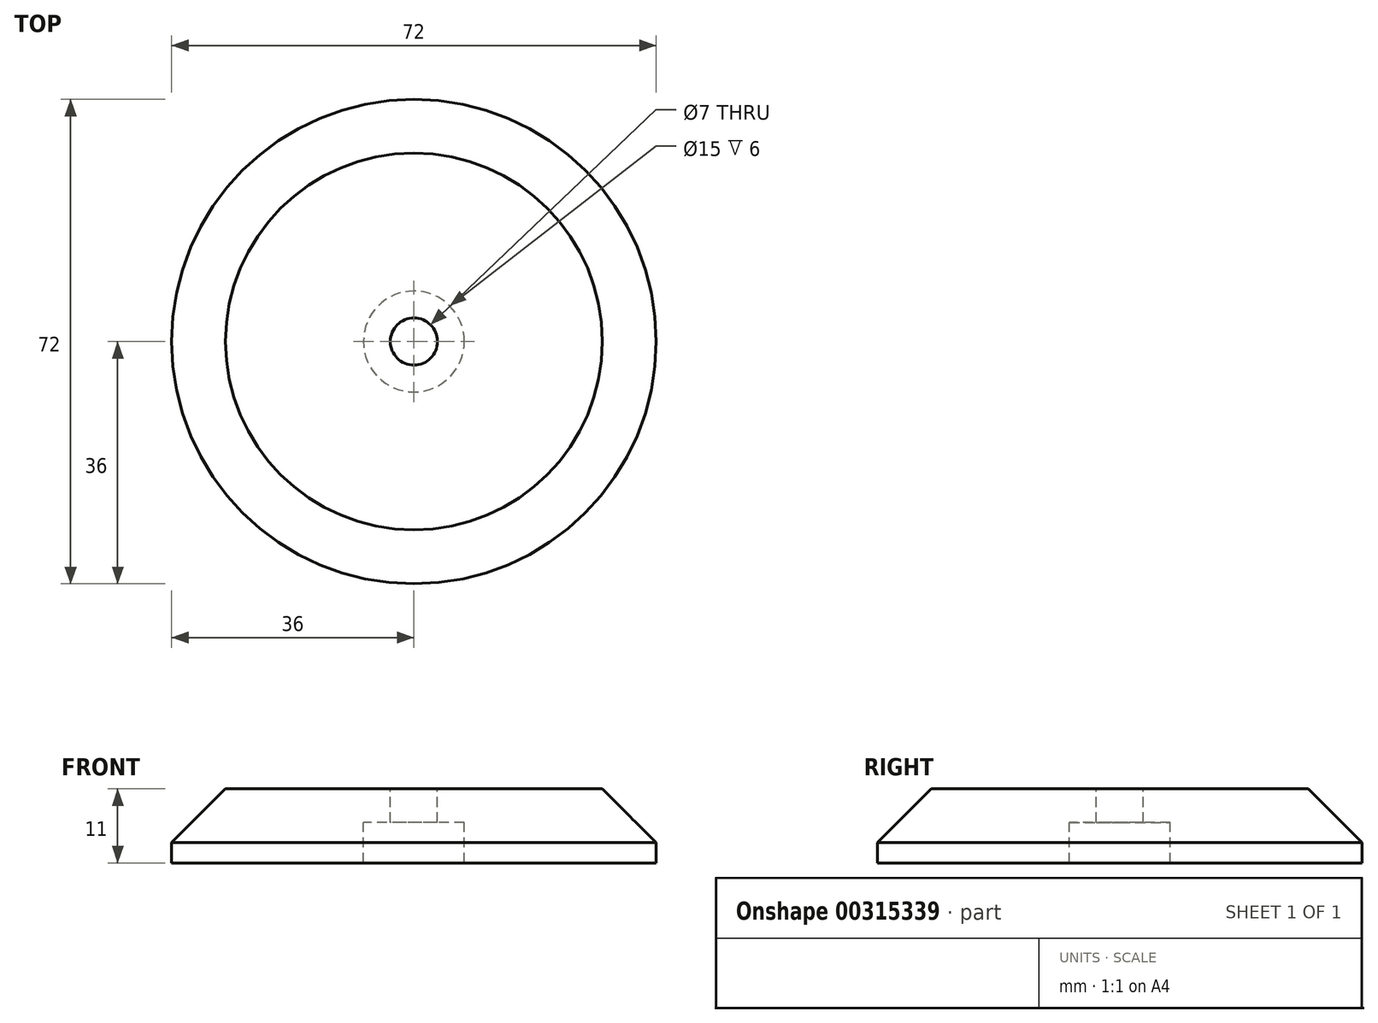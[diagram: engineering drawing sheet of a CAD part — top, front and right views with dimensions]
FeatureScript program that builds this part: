
annotation { "Feature Type Name" : "Feature", "Feature Type Description" : "" }
export const myFeature = defineFeature(function(context is Context, id is Id, definition is map)
    precondition{}
    {
        {
            var Q0;
            Q0=qCreatedBy(makeId("Front.planeOp"),FACE);
            var sketch = newSketch(context, id + "F0", { "sketchPlane" : qUnion([Q0])});
            skLineSegment(sketch, "E0", {"start": v(36, 13.36) * mm, "end": v(36, 13.36) * mm});
            skLineSegment(sketch, "E1", {"start": v(36, 13.36) * mm, "end": v(36, 12.36) * mm});
            skLineSegment(sketch, "E2", {"start": v(36, 12.36) * mm, "end": v(7.5, 12.36) * mm});
            skLineSegment(sketch, "E3", {"start": v(7.5, 12.36) * mm, "end": v(7.5, 18.36) * mm});
            skLineSegment(sketch, "E4", {"start": v(7.5, 18.36) * mm, "end": v(3.5, 18.36) * mm});
            skLineSegment(sketch, "E5", {"start": v(3.5, 18.36) * mm, "end": v(3.5, 23.36) * mm});
            skLineSegment(sketch, "E6", {"start": v(3.5, 23.36) * mm, "end": v(28, 23.36) * mm});
            skLineSegment(sketch, "E7", {"start": v(36, 13.36) * mm, "end": v(36, 15.36) * mm});
            skLineSegment(sketch, "E8", {"start": v(36, 15.36) * mm, "end": v(28, 23.36) * mm});
            skLineSegment(sketch, "E9", {"start": v(0, 30.1) * mm, "end": v(0, 14.94) * mm, "construction": true});
            skSolve(sketch);
        }
        {
            var Q0;
            Q0=makeQuery(id+"F0.imprint","IMPRINT",FACE,{"disambiguationData":[TD([[makeQuery(id+"F0.imprint","IMPRINT",EDGE,{"derivedFrom":sQuery(id+"F0.wireOp",EDGE,"E1")}),-1.0]])]});
            var Q1;
            Q1=sQuery(id+"F0.wireOp",EDGE,"E9");
            revolve(context, id + "F1", {"entities" : qUnion([Q0]), "axis" : qUnion([Q1]), "revolveType" : RevolveType.FULL});
        }
    });
